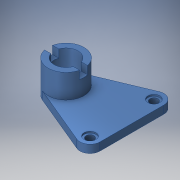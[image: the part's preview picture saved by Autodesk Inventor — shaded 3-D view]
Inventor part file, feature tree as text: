
AUTODESK INVENTOR PART (.ipt)
format: ipt  version: 2016 (Build 200138000, 138)  size: 158,720 bytes
history: native  units: mm
features: extrude x4, sketch x4, hole x1, mirror x1, projected_geometry x1
ambient origin geometry x8: Origin, YZ Plane, XZ Plane, XY Plane, X Axis, Y Axis, Z Axis, Center Point
bodies: Solid1 (feature_tree)
feature tree (11):
  extrude  "Extrusion1"  Depth=80.0mm
  extrude  "Extrusion2"  Depth=12.5mm
  extrude  "Extrusion3"  Depth=30.0mm TaperAngle=0.0deg
  extrude  "Extrusion4"  Depth=30.0mm TaperAngle=0.0deg
  hole  "Hole1"  [1 undecoded]
  mirror  "Mirror1"
  sketch  "Sketch1"  dims[d0=70.0mm d1=80.0mm]
  sketch  "Sketch2"  dims[d2=12.5mm d3=45.0mm]
  projected_geometry  "Projected Loop1"
  sketch  "Sketch3"  dims[d4=10.0mm d5=0.0mm d6=30.0mm d7=0.0mm]
  sketch  "Sketch4"  dims[d8=30.0mm d9=30.0mm d10=0.0mm d14=10.0mm d15=50.0mm d16=3.0mm d17=10.0mm d18=0.0mm d19=10.0mm d20=10.0mm d21=10.0mm d22=6.0mm d23=15.0mm d24=2.0mm d25=90.0deg d26=8.0mm d27=20.594885mm]
note: 1 required parameter value undecoded (feature->parameter linkage not recoverable at this tier; creation-order binding heuristic only, values carry confidence <= 0.55)
